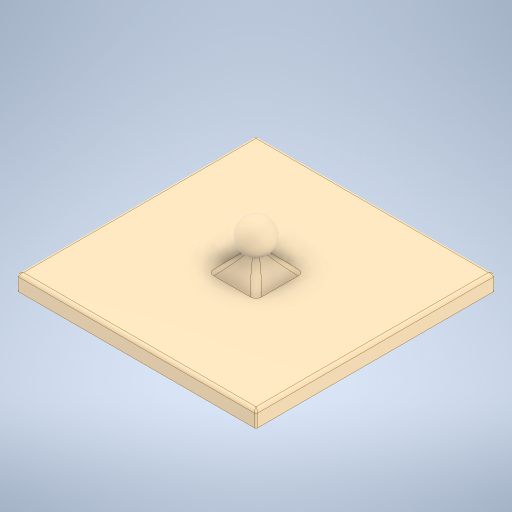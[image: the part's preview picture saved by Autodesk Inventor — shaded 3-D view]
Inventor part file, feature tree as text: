
AUTODESK INVENTOR PART (.ipt)
format: ipt  version: 2023 (Build 270158000, 158)  size: 364,544 bytes
history: native  units: mm
features: sketch x5, fillet x3, extrude x2, plane x2, revolve x1, loft x1, chamfer x1
ambient origin geometry x8: Origin, YZ Plane, XZ Plane, XY Plane, X Axis, Y Axis, Z Axis, Center Point
bodies: Solid1 (feature_tree)
feature tree (15):
  extrude  "Extrusion1"  Depth=150.0mm
  plane  "Work Plane1"
  revolve  "Revolution1"  [1 undecoded]
  sketch  "Sketch6"  dims[d4=10.0mm d5=0.0mm d6=20.0mm d7=20.0mm]
  plane  "Work Plane2"
  loft  "Loft1"
  fillet  "Fillet1"  Radius=20.0mm
  extrude  "Extrusion2"  TaperAngle=90.0deg  [1 undecoded]
  fillet  "Fillet2"  Radius=30.0mm
  fillet  "Fillet3"  Radius=30.0mm
  chamfer  "Chamfer1"  Distance=8.0mm
  sketch  "Sketch1"  dims[d0=150.0mm d1=150.0mm]
  sketch  "Sketch5"  dims[d2=75.0mm d3=75.0mm]
  sketch  "Sketch7"  dims[d8=10.0mm d9=90.0deg d10=30.0mm d11=30.0mm]
  sketch  "Sketch8"  dims[d13=-8.0mm d14=8.0mm d15=0.0mm d16=90.0deg d17=0.0mm d18=90.0deg d19=5.0mm d24=2.0mm d25=0.0mm d26=2.0mm d27=1.0mm d30=2.6mm d31=2.6mm d32=2.6mm d33=2.6mm d34=0.5mm d35=2.0mm d36=45.0deg]
note: 2 required parameter values undecoded (feature->parameter linkage not recoverable at this tier; creation-order binding heuristic only, values carry confidence <= 0.55)